# Revit family: revitupgrade
name_source: partatom
category: Furniture
units: mm (PartAtom-declared; Revit-internal decimal feet)

## family parameters
Always vertical = Yes
Cut with Voids When Loaded = No
Enable Cutting in Views = No
OmniClass Number = 23.40.70.14.64.11
OmniClass Title = Office Furniture
Render Appearance Source = Family Geometry
Room Calculation Point = No
Shared = No
Work Plane-Based = No

## types (1)
- Task Chair
    Arm Finishes = Steelcase - 6053 Seagull
    Assembly Code = E2020200
    Caster/Glide = Steelcase - 6205 Black
    Default Elevation = 0.00 mm
    Description = Steelcase Series 1 delivers on what’s important—performance, style and choice. It retains everything that’s valued in a chair, while making it attainable for everyone.
    Headrest = Steelcase - 6053 Seagull
    Manufacturer = Steelcase
    Release Date = October 2024
    Style Number(s) = 435A00,435A00CN
    URL = https://www.steelcase.com

## geometry (parser evidence)
native form markers: Sweep x4
no freeform markers — native parametric forms only
